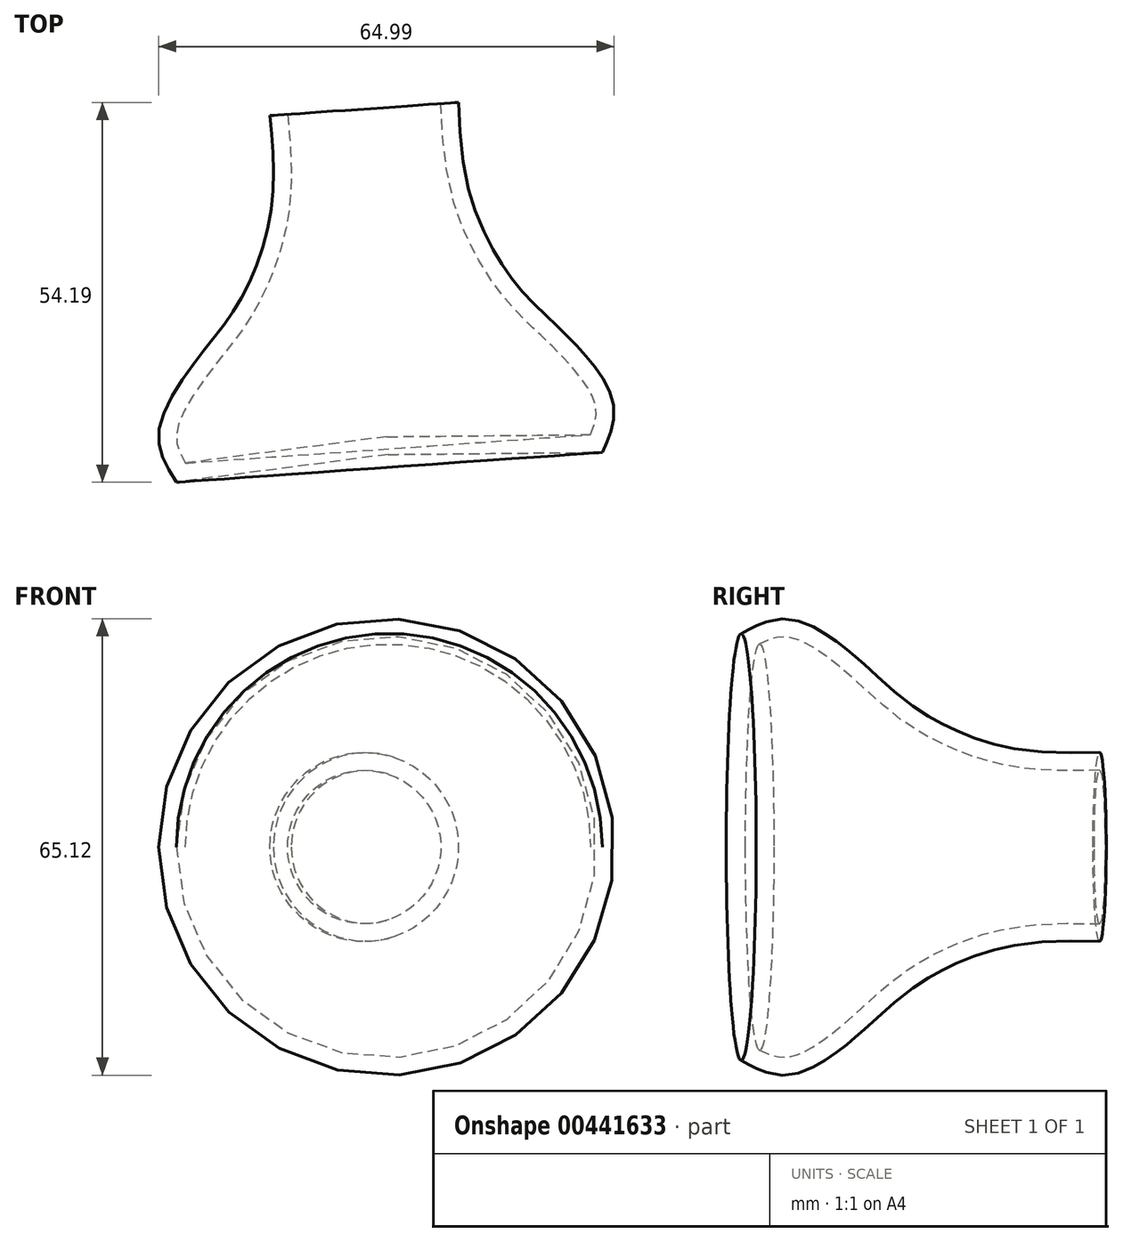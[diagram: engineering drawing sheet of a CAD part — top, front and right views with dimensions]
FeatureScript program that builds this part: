
annotation { "Feature Type Name" : "Feature", "Feature Type Description" : "" }
export const myFeature = defineFeature(function(context is Context, id is Id, definition is map)
    precondition{}
    {
        {
            var Q0;
            Q0=qCreatedBy(makeId("Top.planeOp"),FACE);
            var sketch = newSketch(context, id + "F0", { "sketchPlane" : qUnion([Q0])});
            skLineSegment(sketch, "E0", {"start": v(-31.8, 38.36) * mm, "end": v(-28.35, -10.93) * mm});
            skLineSegment(sketch, "E1", {"start": v(-31.8, 38.36) * mm, "end": v(-18.35, 39.3) * mm});
            skFitSpline(sketch, "E2", {"points": [v(-18.35, 39.3) * mm, v(-16.63, 25.9) * mm, v(-10.62, 14.02) * mm, v(-3.85, 6.96) * mm, v(3.66, -3.26) * mm, v(2.16, -10.62) * mm], "startDerivative": vector(2.93, -61.4) * mm, "endDerivative": vector(-19.59, -43.35) * mm});
            skFitSpline(sketch, "E3", {"points": [v(-28.35, -10.93) * mm, v(2.16, -10.62) * mm], "startDerivative": vector(30.5, 0.3) * mm, "endDerivative": vector(30.5, 0.3) * mm});
            skPoint(sketch, "E4.start.orphan", {"position": v(-28.35, -35.07) * mm});
            skLineSegment(sketch, "E5", {"start": v(-31.8, 38.36) * mm, "end": v(-32.61, 49.9) * mm});
            skLineSegment(sketch, "E6", {"start": v(-31.8, 38.36) * mm, "end": v(-27.35, -25.2) * mm});
            skSolve(sketch);
        }
        {
            var Q0;
            Q0 = qSketchRegion(id + "F0", true);
            var Q1;
            Q1=sQuery(id+"F0.wireOp",EDGE,"E6");
            revolve(context, id + "F1", {"entities" : qUnion([Q0]), "axis" : qUnion([Q1]), "revolveType" : RevolveType.FULL});
        }
        {
            var Q0;
            Q0=makeQuery(id+"F1.opRevolve","SWEPT_FACE",FACE,{"disambiguationData":[OSD([sQuery(id+"F0.wireOp",EDGE,"E1")])]});
            shell(context, id + "F2", {"entities" : qUnion([Q0]), "thickness" : 2.54 * mm});
        }
    });
